# Revit family: Zumtobel eBox
name_source: partatom
category: Lighting Fixtures
revit_build: Autodesk Revit 2016 (Build: 20150220_1215(x64)
units: mm (PartAtom-declared; Revit-internal decimal feet)

## family parameters
Always vertical = Yes
Cut with Voids When Loaded = No
Light Source = No
Part Type = Normal
Room Calculation Point = No
Round Connector Dimension = Use Diameter
Shared = No
Work Plane-Based = No

## types (3) — shared parameters
Body = ZG_Metal_White
Description = Central emergency lighting unit
Fitting = ZG_Plastic_Black
Manufacturer = Zumtobel Lighting
URL = http://www.zumtobel.com
Voltage = 230 V

## per-type parameters (varying)
| type | Apparent Load | Cover | Depth | Height | Model | Onlite eBox | Onlite eBox SUB | Width |
| ONLITE central eBox MS1200 | 5500 VA | ZG_Plastics_Transparent | 250 mm  [stored 0.82021 ft] | 1200 mm | 22176359 | Yes | No | 600 mm |
| ONLITE central eBox MS1700 | 5500 VA | ZG_Plastics_Transparent | 250 mm  [stored 0.82021 ft] | 1690 mm  [stored 5.54462 ft] | 22176472 | Yes | No | 600 mm |
| ONLITE central eBox SUB | 1000 VA | ZG_Plastic_Black | 164 mm  [stored 0.538058 ft] | 370 mm  [stored 1.21391 ft] | 22185290 | No | Yes | 300 mm |

note: [stored X ft] marks values corroborated as IEEE doubles in the binary element streams (Revit-internal decimal feet)

## geometry (parser evidence)
native form markers: Blend x6, Sweep x5
no freeform markers — native parametric forms only
